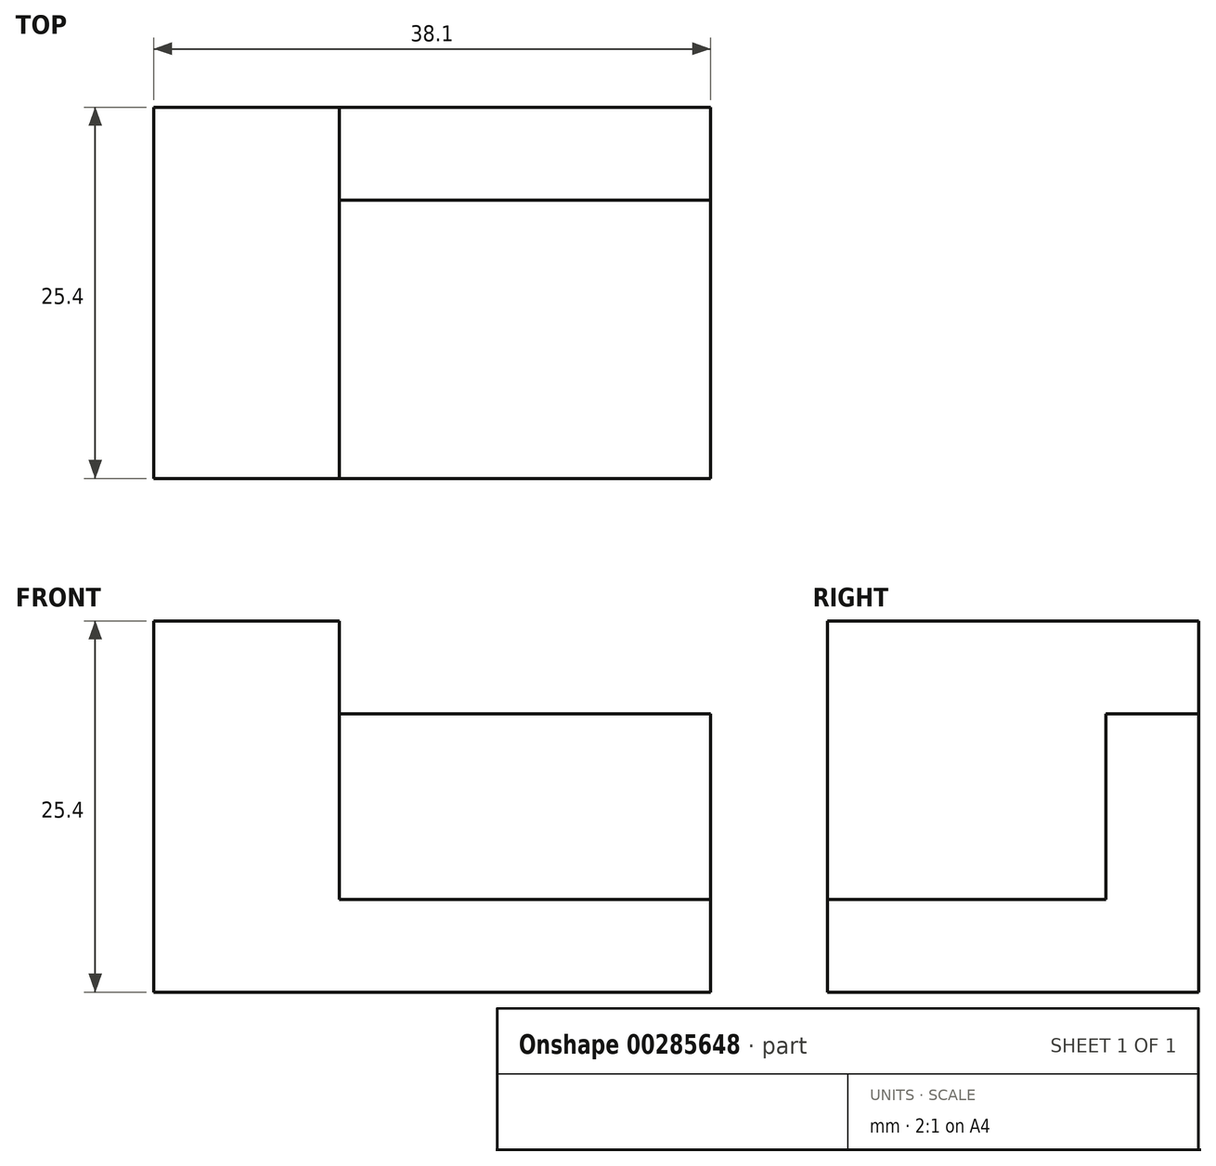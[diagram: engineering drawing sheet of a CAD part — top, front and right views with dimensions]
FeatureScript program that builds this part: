
annotation { "Feature Type Name" : "Feature", "Feature Type Description" : "" }
export const myFeature = defineFeature(function(context is Context, id is Id, definition is map)
    precondition{}
    {
        {
            var Q0;
            Q0=qCreatedBy(makeId("Front.planeOp"),FACE);
            var sketch = newSketch(context, id + "F0", { "sketchPlane" : qUnion([Q0])});
            skLineSegment(sketch, "E0", {"start": v(0, 0) * mm, "end": v(0, 25.4) * mm});
            skLineSegment(sketch, "E1", {"start": v(0, 25.4) * mm, "end": v(12.7, 25.4) * mm});
            skLineSegment(sketch, "E2", {"start": v(12.7, 25.4) * mm, "end": v(12.7, 6.35) * mm});
            skLineSegment(sketch, "E3", {"start": v(12.7, 6.35) * mm, "end": v(38.1, 6.35) * mm});
            skLineSegment(sketch, "E4", {"start": v(38.1, 6.35) * mm, "end": v(38.1, 0) * mm});
            skLineSegment(sketch, "E5", {"start": v(38.1, 0) * mm, "end": v(0, 0) * mm});
            skSolve(sketch);
        }
        {
            var Q0;
            Q0 = qSketchRegion(id + "F0", true);
            extrude(context, id + "F1", {"entities" : qUnion([Q0]), "depth" : 25.4 * mm});
        }
        {
            var Q0;
            Q0=makeQuery(id+"F1.opExtrude","SWEPT_FACE",FACE,{"disambiguationData":[OSD([sQuery(id+"F0.wireOp",EDGE,"E2")])]});
            var sketch = newSketch(context, id + "F2", { "sketchPlane" : qUnion([Q0])});
            skLineSegment(sketch, "E6", {"start": v(-6.35, 6.35) * mm, "end": v(-6.35, 19.05) * mm});
            skLineSegment(sketch, "E7", {"start": v(-6.35, 19.05) * mm, "end": v(0, 19.05) * mm});
            skSolve(sketch);
        }
        {
            var Q0;
            Q0 = qSketchRegion(id + "F2", true);
            var Q1;
            {var subQ0=sQuery(id+"F2.wireOp",EDGE,"E6");Q1=makeQuery(id+"F2.imprint","IMPRINT",FACE,{"disambiguationData":[TD([[makeQuery(id+"F2.imprint","IMPRINT",EDGE,{"derivedFrom":subQ0}),-1.0]])]});}
            extrude(context, id + "F3", {"entities" : qUnion([Q0, Q1]), "operationType" : NewBodyOperationType.ADD, "depth" : 25.4 * mm});
        }
    });
